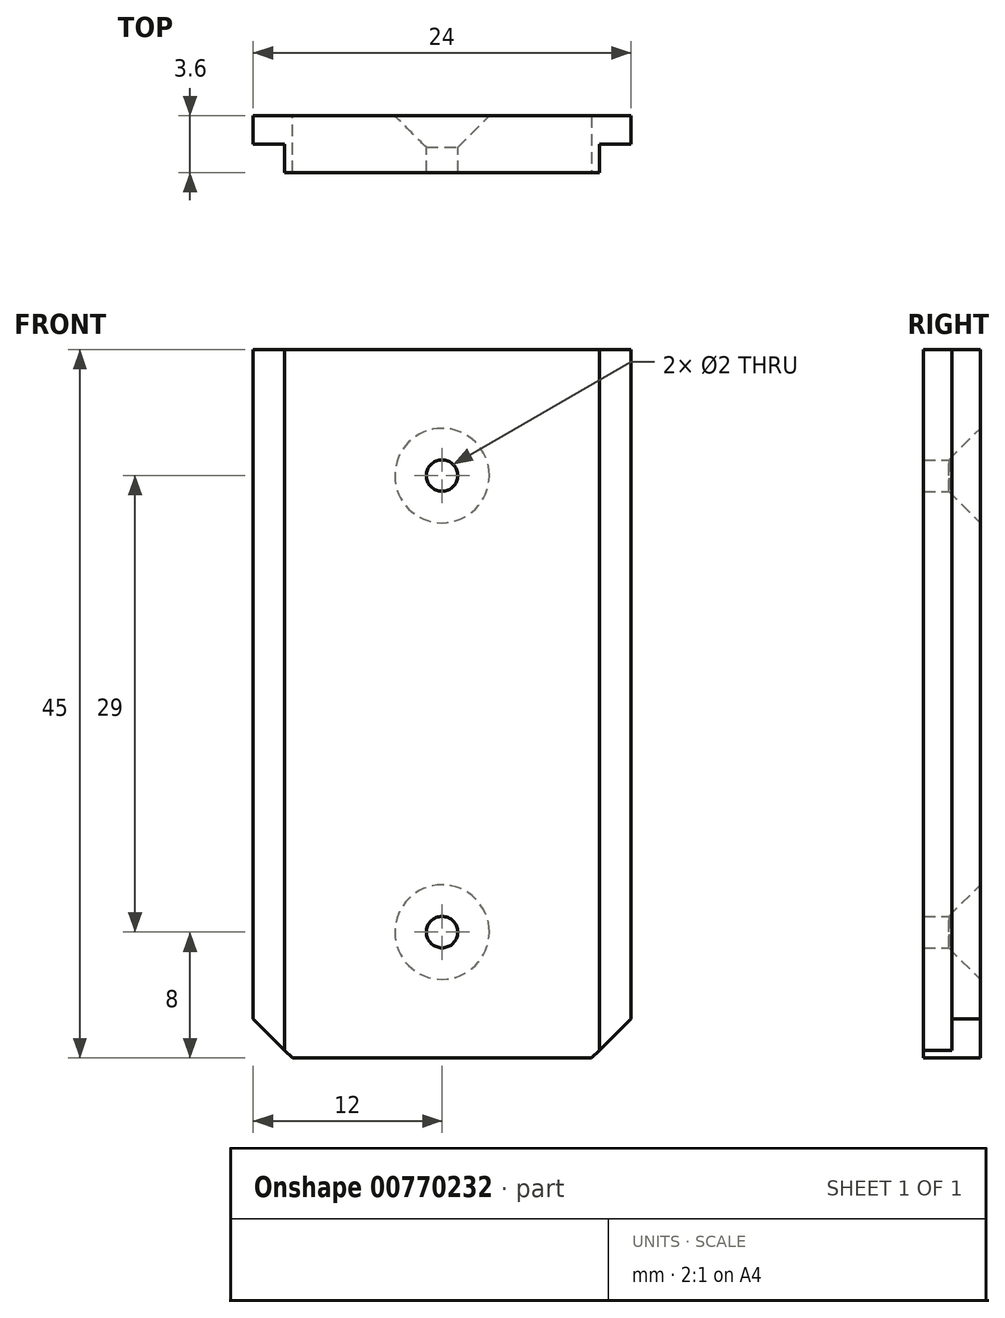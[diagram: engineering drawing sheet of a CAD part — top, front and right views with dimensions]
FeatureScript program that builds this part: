
annotation { "Feature Type Name" : "Feature", "Feature Type Description" : "" }
export const myFeature = defineFeature(function(context is Context, id is Id, definition is map)
    precondition{}
    {
        {
            var Q0;
            Q0=qCreatedBy(makeId("Top.planeOp"),FACE);
            var sketch = newSketch(context, id + "F0", { "sketchPlane" : qUnion([Q0])});
            skLineSegment(sketch, "E0.bottom", {"start": v(-12, 3.4) * mm, "end": v(12, 3.4) * mm});
            skLineSegment(sketch, "E0.top", {"start": v(-12, 1.6) * mm, "end": v(12, 1.6) * mm});
            skLineSegment(sketch, "E0.left", {"start": v(-12, 3.4) * mm, "end": v(-12, 1.6) * mm});
            skLineSegment(sketch, "E0.right", {"start": v(12, 3.4) * mm, "end": v(12, 1.6) * mm});
            skLineSegment(sketch, "E1.bottom", {"start": v(-10, 1.6) * mm, "end": v(10, 1.6) * mm});
            skLineSegment(sketch, "E1.top", {"start": v(-10, -0.2) * mm, "end": v(10, -0.2) * mm});
            skLineSegment(sketch, "E1.left", {"start": v(-10, 1.6) * mm, "end": v(-10, -0.2) * mm});
            skLineSegment(sketch, "E1.right", {"start": v(10, 1.6) * mm, "end": v(10, -0.2) * mm});
            skSolve(sketch);
        }
        {
            var Q0;
            Q0 = qSketchRegion(id + "F0", true);
            extrude(context, id + "F1", {"entities" : qUnion([Q0]), "depth" : 45 * mm, "offsetDistance" : 25 * mm});
        }
        {
            var Q0;
            Q0=makeQuery(id+"F1.opExtrude","CAP_EDGE",EDGE,{"disambiguationData":[OSD([sQuery(id+"F0.wireOp",EDGE,"E0.right")])],"isStart":true});
            chamfer(context, id + "F2", {"entities" : qUnion([Q0]), "width" : 2.5 * mm, "tangentPropagation" : true});
        }
        {
            var Q0;
            Q0=makeQuery(id+"F1.opExtrude","CAP_EDGE",EDGE,{"disambiguationData":[OSD([sQuery(id+"F0.wireOp",EDGE,"E0.left")])],"isStart":true});
            chamfer(context, id + "F3", {"entities" : qUnion([Q0]), "width" : 2.5 * mm, "tangentPropagation" : true});
        }
        {
            var Q0;
            Q0=makeQuery(id+"F1.opExtrude","SWEPT_FACE",FACE,{"disambiguationData":[OSD([sQuery(id+"F0.wireOp",EDGE,"E0.bottom")])]});
            var sketch = newSketch(context, id + "F4", { "sketchPlane" : qUnion([Q0])});
            skPoint(sketch, "E2", {"position": v(0, 37) * mm});
            skPoint(sketch, "E3", {"position": v(0, 8) * mm});
            skSolve(sketch);
        }
        {
            var Q0;
            Q0=sQuery(id+"F4.wireOp",VERTEX,"E2");
            var Q1;
            Q1=sQuery(id+"F4.wireOp",VERTEX,"E3");
            var Q2;
            Q2=makeQuery(id+"F1.opExtrude","SWEPT_BODY",BODY,{"disambiguationData":[OSD([sQuery(id+"F0.wireOp",EDGE,"E0.bottom"),sQuery(id+"F0.wireOp",EDGE,"E0.top"),sQuery(id+"F0.wireOp",EDGE,"E0.left"),sQuery(id+"F0.wireOp",EDGE,"E0.right"),sQuery(id+"F0.wireOp",EDGE,"E1.top"),sQuery(id+"F0.wireOp",EDGE,"E1.left"),sQuery(id+"F0.wireOp",EDGE,"E1.right")])]});
            hole(context, id + "F5", {"style" : HoleStyle.C_SINK, "endStyle" : HoleEndStyle.BLIND, "holeDiameter" : 2 * mm, "cSinkDiameter" : 6 * mm, "cSinkAngle" : 90 * degree, "majorDiameter" : 5 * mm, "holeDepth" : 15 * mm, "isTappedThrough" : true, "tappedDepth" : 12 * mm, "tapClearance" : 3, "locations" : qUnion([Q0, Q1]), "scope" : qUnion([Q2])});
        }
    });
